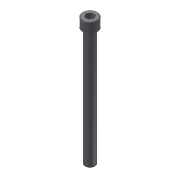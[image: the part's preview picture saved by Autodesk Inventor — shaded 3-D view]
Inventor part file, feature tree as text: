
AUTODESK INVENTOR PART (.ipt)
format: ipt  version: 2012 (Build 160160000, 160)  size: 99,328 bytes
history: native  units: in
note: dims shown in document units (in); Inventor stores cm internally (conversion verified against a paired STEP export)
features: extrude x3, sketch x3, fillet x1
ambient origin geometry x8: Origin, YZ Plane, XZ Plane, XY Plane, X Axis, Y Axis, Z Axis, Center Point
bodies: Solid1 (feature_tree)
feature tree (7):
  extrude  "Extrusion1"  Depth=3.0in TaperAngle=0.0deg
  extrude  "Extrusion2"  Depth=0.25in TaperAngle=0.0deg
  extrude  "Extrusion3"  Depth=0.125in TaperAngle=0.0deg
  fillet  "Fillet1"  Radius=0.0156in
  sketch  "Sketch1"  dims[d0=0.25in d1=3.0in d2=0.0in]
  sketch  "Sketch2"  dims[d3=0.375in d4=0.25in d5=0.0in]
  sketch  "Sketch3"  dims[d6=0.1875in d7=0.125in d8=0.0in d9=0.0156in]
